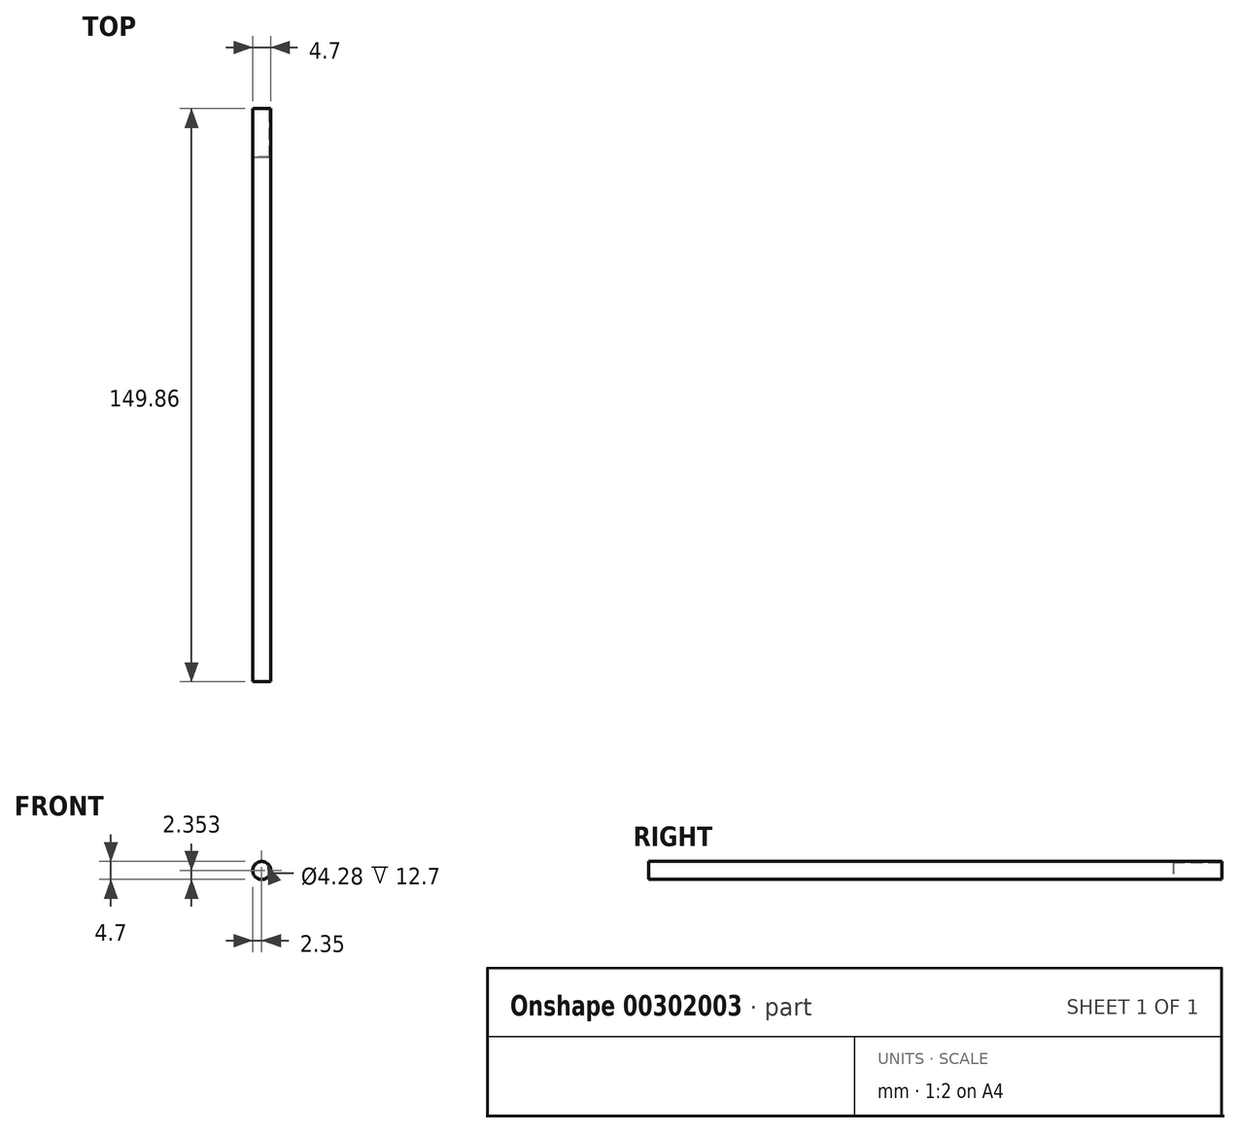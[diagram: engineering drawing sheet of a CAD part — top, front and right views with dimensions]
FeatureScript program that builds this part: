
annotation { "Feature Type Name" : "Feature", "Feature Type Description" : "" }
export const myFeature = defineFeature(function(context is Context, id is Id, definition is map)
    precondition{}
    {
        {
            var Q0;
            Q0=qCreatedBy(makeId("Front.planeOp"),FACE);
            var sketch = newSketch(context, id + "F0", { "sketchPlane" : qUnion([Q0])});
            skCircle(sketch, "E0", {"center": v(51.39, 26.42) * mm, "radius": 2.35 * mm});
            skSolve(sketch);
        }
        {
            var Q0;
            Q0 = qSketchRegion(id + "F0", true);
            extrude(context, id + "F1", {"entities" : qUnion([Q0]), "oppositeDirection" : true, "depth" : 149.86 * mm});
        }
        {
            var Q0;
            Q0=makeQuery(id+"F1.opExtrude","CAP_FACE",FACE,{"disambiguationData":[OSD([sQuery(id+"F0.wireOp",EDGE,"E0")])],"isStart":false});
            var sketch = newSketch(context, id + "F2", { "sketchPlane" : qUnion([Q0])});
            skPoint(sketch, "E1", {"position": v(-51.39, 26.42) * mm});
            skCircle(sketch, "E2", {"center": v(-51.39, 26.42) * mm, "radius": 2.14 * mm});
            skCircle(sketch, "E3", {"center": v(-51.39, 26.42) * mm, "radius": 2.38 * mm});
            skCircle(sketch, "E4", {"center": v(-51.39, 26.42) * mm, "radius": 2.42 * mm});
            skSolve(sketch);
        }
        {
            var Q0;
            Q0=makeQuery(id+"F2.imprint","IMPRINT",FACE,{"disambiguationData":[TD([[makeQuery(id+"F2.imprint","IMPRINT",EDGE,{"derivedFrom":sQuery(id+"F2.wireOp",EDGE,"E2")}),1.0]])]});
            extrude(context, id + "F3", {"entities" : qUnion([Q0]), "operationType" : NewBodyOperationType.REMOVE, "oppositeDirection" : true, "depth" : 12.7 * mm});
        }
        {
            var Q0;
            Q0=sQuery(id+"F2.wireOp",EDGE,"E3");
            extrude(context, id + "F4", {"bodyType" : ToolBodyType.SURFACE, "surfaceEntities" : qUnion([Q0]), "oppositeDirection" : true, "depth" : 7.87 * mm});
        }
        {
            var Q0;
            Q0=sQuery(id+"F2.wireOp",EDGE,"E4");
            extrude(context, id + "F5", {"bodyType" : ToolBodyType.SURFACE, "surfaceEntities" : qUnion([Q0]), "oppositeDirection" : true, "depth" : 0.53 * mm});
        }
    });
